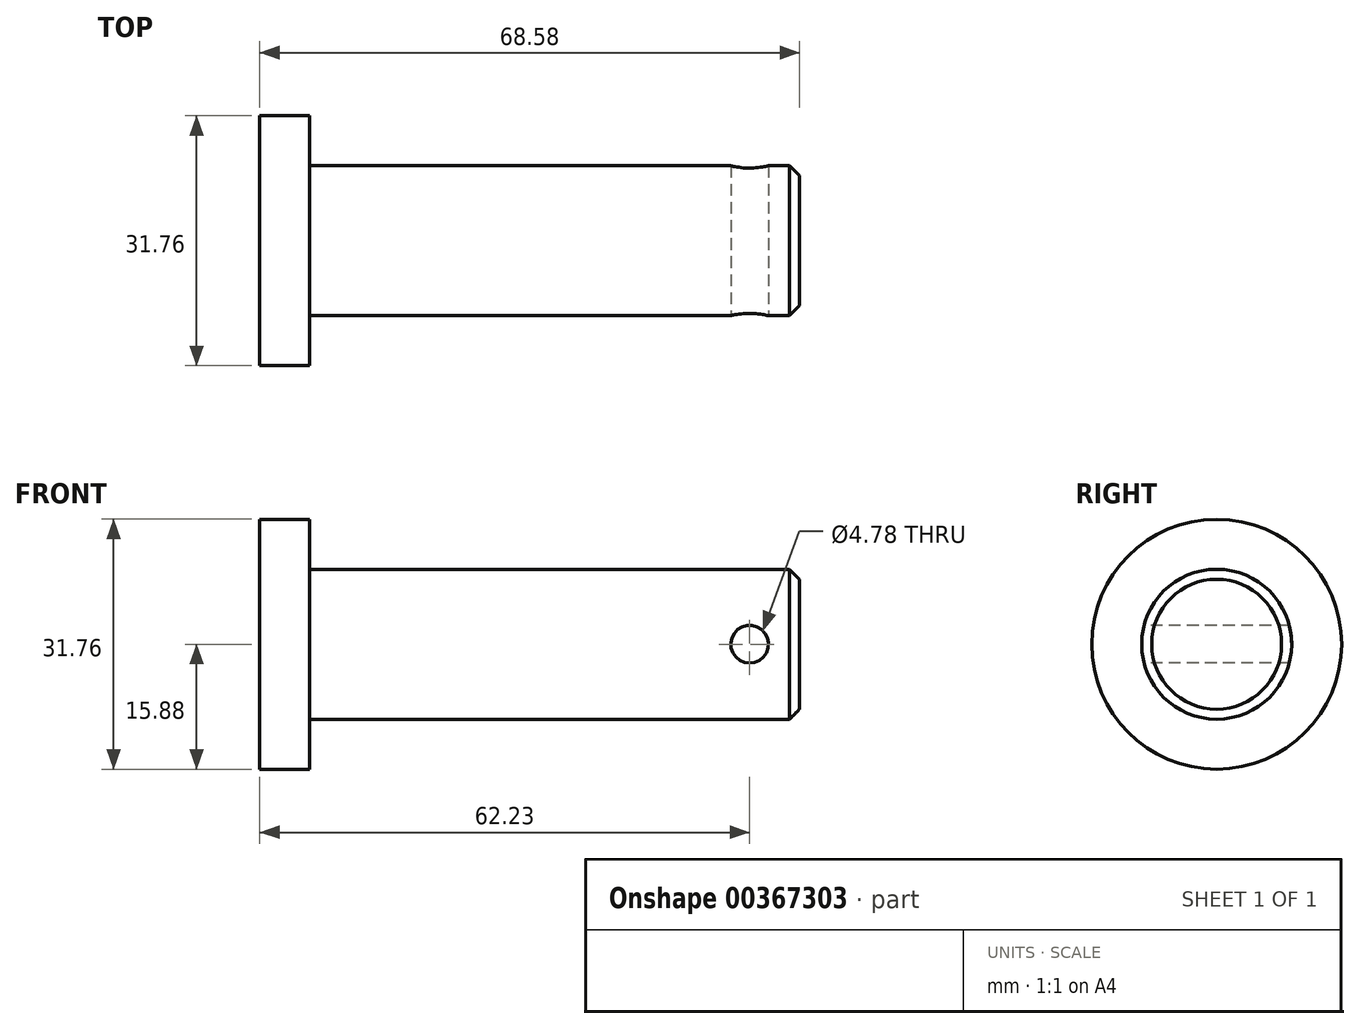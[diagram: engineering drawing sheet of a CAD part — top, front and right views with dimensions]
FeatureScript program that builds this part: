
annotation { "Feature Type Name" : "Feature", "Feature Type Description" : "" }
export const myFeature = defineFeature(function(context is Context, id is Id, definition is map)
    precondition{}
    {
        {
            var Q0;
            Q0=qCreatedBy(makeId("Right.planeOp"),FACE);
            var sketch = newSketch(context, id + "F0", { "sketchPlane" : qUnion([Q0])});
            skCircle(sketch, "E0", {"center": v(0, 0) * mm, "radius": 15.88 * mm});
            skSolve(sketch);
        }
        {
            var Q0;
            Q0 = qSketchRegion(id + "F0", true);
            extrude(context, id + "F1", {"entities" : qUnion([Q0]), "depth" : 6.35 * mm});
        }
        {
            var Q0;
            Q0=makeQuery(id+"F1.opExtrude","CAP_FACE",FACE,{"disambiguationData":[OSD([sQuery(id+"F0.wireOp",EDGE,"E0")])],"isStart":false});
            var sketch = newSketch(context, id + "F2", { "sketchPlane" : qUnion([Q0])});
            skCircle(sketch, "E1", {"center": v(0, 0) * mm, "radius": 9.53 * mm});
            skSolve(sketch);
        }
        {
            var Q0;
            Q0 = qSketchRegion(id + "F2", true);
            extrude(context, id + "F3", {"entities" : qUnion([Q0]), "operationType" : NewBodyOperationType.ADD, "depth" : 62.23 * mm});
        }
        {
            var Q0;
            Q0=makeQuery(id+"F3.opExtrude","CAP_EDGE",EDGE,{"disambiguationData":[OSD([sQuery(id+"F2.wireOp",EDGE,"E1")])],"isStart":false});
            chamfer(context, id + "F4", {"entities" : qUnion([Q0]), "chamferType" : ChamferType.OFFSET_ANGLE, "width" : 1.27 * mm, "oppositeDirection" : false, "angle" : 45 * degree, "tangentPropagation" : true});
        }
        {
            var Q0;
            Q0=qCreatedBy(makeId("Front.planeOp"),FACE);
            var sketch = newSketch(context, id + "F5", { "sketchPlane" : qUnion([Q0])});
            skCircle(sketch, "E2", {"center": v(62.23, 0) * mm, "radius": 2.39 * mm});
            skSolve(sketch);
        }
        {
            var Q0;
            Q0 = qSketchRegion(id + "F5", true);
            extrude(context, id + "F6", {"entities" : qUnion([Q0]), "operationType" : NewBodyOperationType.REMOVE, "endBound" : BoundingType.SYMMETRIC, "oppositeDirection" : true, "depth" : 19.05 * mm});
        }
    });
